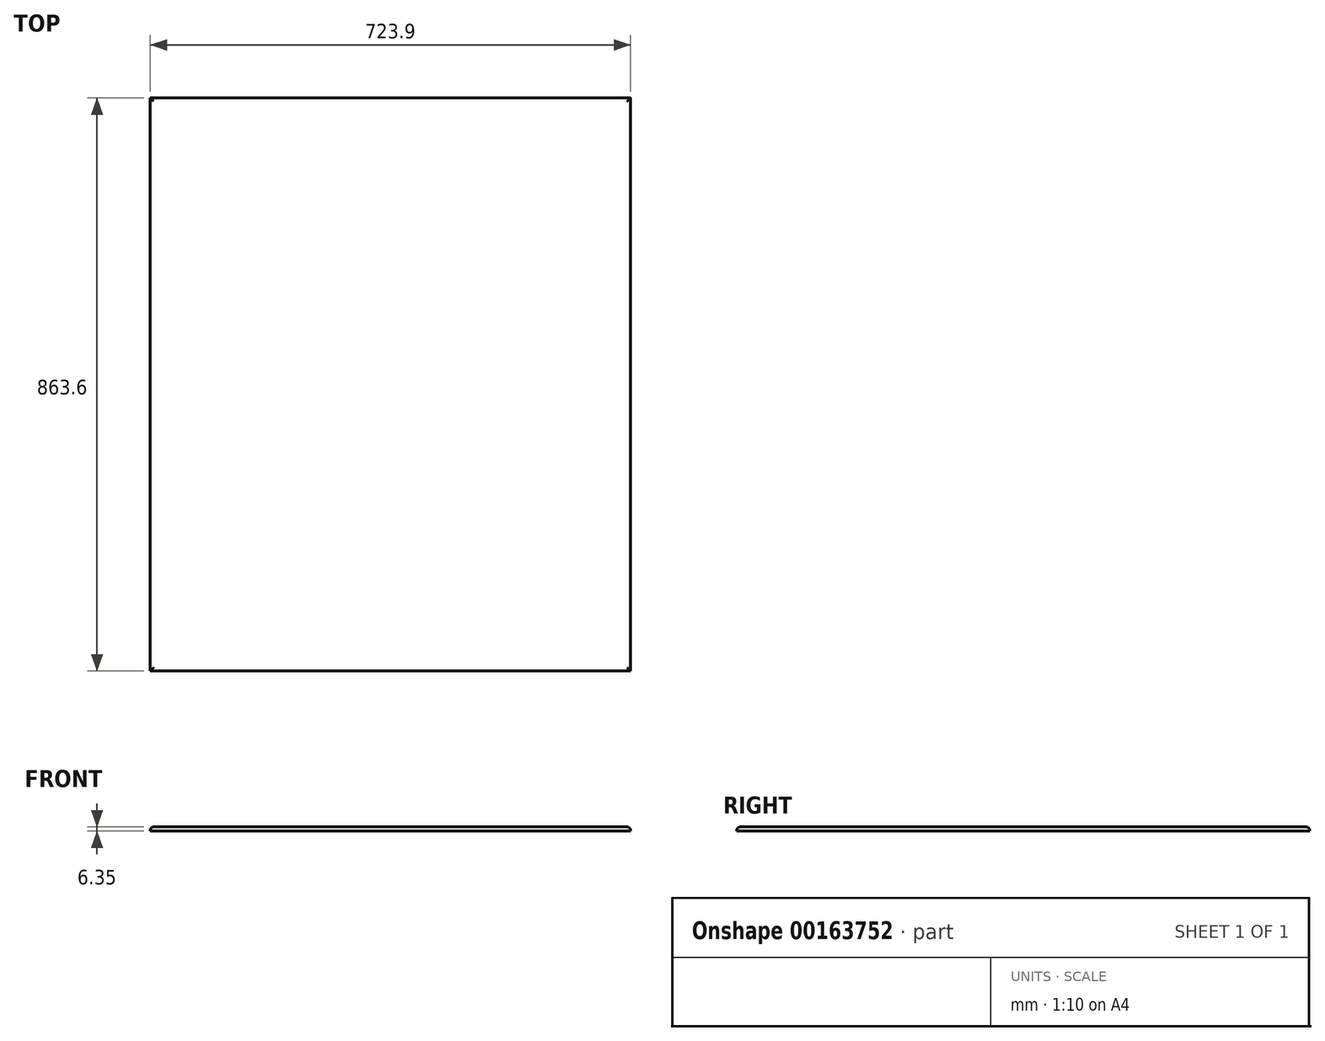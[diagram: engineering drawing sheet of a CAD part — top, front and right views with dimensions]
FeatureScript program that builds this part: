
annotation { "Feature Type Name" : "Feature", "Feature Type Description" : "" }
export const myFeature = defineFeature(function(context is Context, id is Id, definition is map)
    precondition{}
    {
        {
            var Q0;
            Q0=qCreatedBy(makeId("Top.planeOp"),FACE);
            var sketch = newSketch(context, id + "F0", { "sketchPlane" : qUnion([Q0])});
            skLineSegment(sketch, "E0.bottom", {"start": v(361.95, 431.8) * mm, "end": v(-361.95, 431.8) * mm});
            skLineSegment(sketch, "E0.top", {"start": v(361.95, -431.8) * mm, "end": v(-361.95, -431.8) * mm});
            skLineSegment(sketch, "E0.left", {"start": v(361.95, 431.8) * mm, "end": v(361.95, -431.8) * mm});
            skLineSegment(sketch, "E0.right", {"start": v(-361.95, 431.8) * mm, "end": v(-361.95, -431.8) * mm});
            skPoint(sketch, "E0.middle", {"position": v(0, 0) * mm});
            skSolve(sketch);
        }
        {
            var Q0;
            Q0 = qSketchRegion(id + "F0", true);
            extrude(context, id + "F1", {"entities" : qUnion([Q0]), "depth" : 6.35 * mm, "offsetDistance" : 25.4 * mm});
        }
        {
            var Q0;
            Q0=makeQuery(id+"F1.opExtrude","CAP_FACE",FACE,{"disambiguationData":[OSD([sQuery(id+"F0.wireOp",EDGE,"E0.bottom"),sQuery(id+"F0.wireOp",EDGE,"E0.top"),sQuery(id+"F0.wireOp",EDGE,"E0.left"),sQuery(id+"F0.wireOp",EDGE,"E0.right")])],"isStart":false});
            fillet(context, id + "F2", {"entities" : qUnion([Q0]), "radius" : 5.08 * mm, "tangentPropagation" : true, "allowEdgeOverflow" : false});
        }
    });
